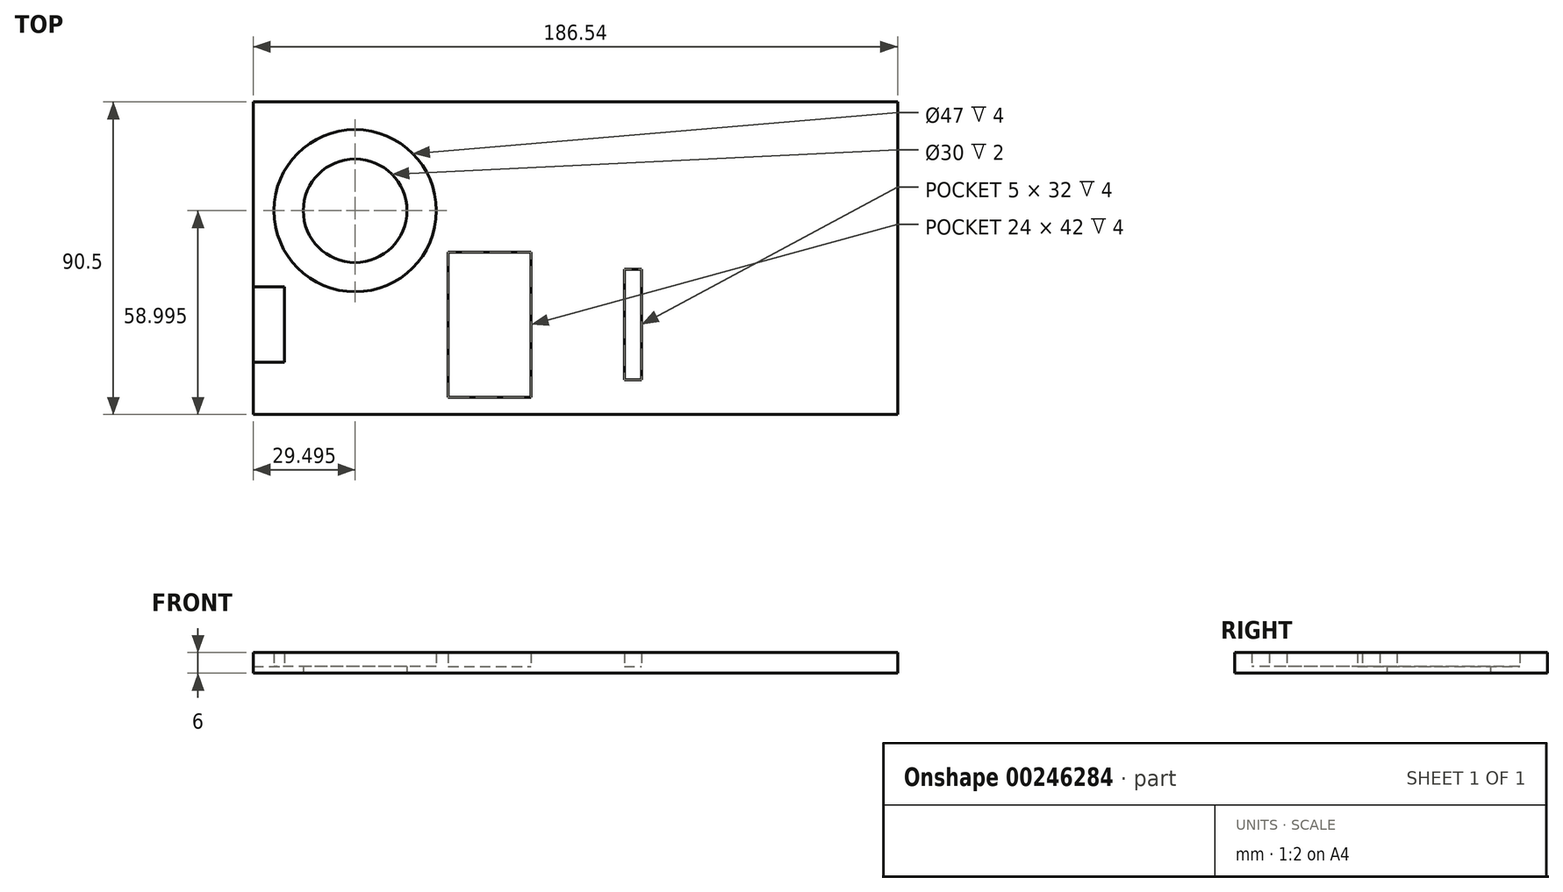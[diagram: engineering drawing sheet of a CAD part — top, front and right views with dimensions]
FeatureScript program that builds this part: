
annotation { "Feature Type Name" : "Feature", "Feature Type Description" : "" }
export const myFeature = defineFeature(function(context is Context, id is Id, definition is map)
    precondition{}
    {
        {
            var Q0;
            Q0=qCreatedBy(makeId("Top.planeOp"),FACE);
            var sketch = newSketch(context, id + "F0", { "sketchPlane" : qUnion([Q0])});
            skLineSegment(sketch, "E0.bottom", {"start": v(-93.27, 69.1) * mm, "end": v(93.27, 69.1) * mm});
            skLineSegment(sketch, "E0.top", {"start": v(-93.27, -21.4) * mm, "end": v(93.27, -21.4) * mm});
            skLineSegment(sketch, "E0.left", {"start": v(-93.27, 69.1) * mm, "end": v(-93.27, -21.4) * mm});
            skLineSegment(sketch, "E0.right", {"start": v(93.27, 69.1) * mm, "end": v(93.27, -21.4) * mm});
            skPoint(sketch, "E1", {"position": v(0, 69.1) * mm});
            skCircle(sketch, "E2", {"center": v(-63.77, 37.6) * mm, "radius": 26.5 * mm, "construction": true});
            skLineSegment(sketch, "E3", {"start": v(-52.33, 4.6) * mm, "end": v(-1.02, 4.6) * mm, "construction": true});
            skLineSegment(sketch, "E4.bottom", {"start": v(-79.77, 13.6) * mm, "end": v(-47.77, 13.6) * mm, "construction": true});
            skLineSegment(sketch, "E4.top", {"start": v(-79.77, -4.4) * mm, "end": v(-47.77, -4.4) * mm, "construction": true});
            skLineSegment(sketch, "E4.left", {"start": v(-79.77, 13.6) * mm, "end": v(-79.77, -4.4) * mm, "construction": true});
            skLineSegment(sketch, "E4.right", {"start": v(-47.77, 13.6) * mm, "end": v(-47.77, -4.4) * mm, "construction": true});
            skPoint(sketch, "E5", {"position": v(-47.77, 4.6) * mm});
            skPoint(sketch, "E6", {"position": v(-63.77, -4.4) * mm});
            skLineSegment(sketch, "E7.bottom", {"start": v(14.17, 20.6) * mm, "end": v(19.17, 20.6) * mm});
            skLineSegment(sketch, "E7.top", {"start": v(14.17, -11.4) * mm, "end": v(19.17, -11.4) * mm});
            skLineSegment(sketch, "E7.left", {"start": v(14.17, 20.6) * mm, "end": v(14.17, -11.4) * mm});
            skLineSegment(sketch, "E7.right", {"start": v(93.27, 20.6) * mm, "end": v(93.27, -11.4) * mm});
            skLineSegment(sketch, "E8.bottom", {"start": v(-93.27, 15.5) * mm, "end": v(-84.27, 15.5) * mm});
            skLineSegment(sketch, "E8.top", {"start": v(-93.27, -6.29) * mm, "end": v(-84.27, -6.29) * mm});
            skLineSegment(sketch, "E8.left", {"start": v(-93.27, 15.5) * mm, "end": v(-93.27, -6.29) * mm});
            skLineSegment(sketch, "E8.right", {"start": v(-84.27, 15.5) * mm, "end": v(-84.27, -6.29) * mm});
            skPoint(sketch, "E9", {"position": v(-84.27, 4.6) * mm});
            skPoint(sketch, "E10.firstSnap0", {"position": v(-88.77, 15.5) * mm});
            skLineSegment(sketch, "E11.bottom", {"start": v(-15.83, 13.6) * mm, "end": v(14.17, 13.6) * mm, "construction": true});
            skLineSegment(sketch, "E11.top", {"start": v(-15.83, -4.4) * mm, "end": v(14.17, -4.4) * mm, "construction": true});
            skLineSegment(sketch, "E11.left", {"start": v(-15.83, 13.6) * mm, "end": v(-15.83, -4.4) * mm});
            skLineSegment(sketch, "E11.right", {"start": v(14.17, 13.6) * mm, "end": v(14.17, -4.4) * mm});
            skPoint(sketch, "E12", {"position": v(14.17, 4.6) * mm});
            skPoint(sketch, "E13", {"position": v(93.27, 4.6) * mm});
            skLineSegment(sketch, "E14.bottom", {"start": v(-33.83, 25.6) * mm, "end": v(-15.83, 25.6) * mm});
            skLineSegment(sketch, "E14.top", {"start": v(-33.83, -16.4) * mm, "end": v(-15.83, -16.4) * mm});
            skLineSegment(sketch, "E14.left", {"start": v(-33.83, 25.6) * mm, "end": v(-33.83, -16.4) * mm, "construction": true});
            skLineSegment(sketch, "E14.right", {"start": v(-15.83, 25.6) * mm, "end": v(-15.83, -16.4) * mm, "construction": true});
            skPoint(sketch, "E15", {"position": v(-33.83, 4.6) * mm});
            skLineSegment(sketch, "E16.left", {"start": v(-47.77, 9.6) * mm, "end": v(-47.77, -0.4) * mm});
            skLineSegment(sketch, "E16.right", {"start": v(-33.83, 9.6) * mm, "end": v(-33.83, -0.4) * mm});
            skLineSegment(sketch, "E17", {"start": v(-15.83, 25.6) * mm, "end": v(-12.83, 25.6) * mm});
            skLineSegment(sketch, "E18", {"start": v(-12.83, 25.6) * mm, "end": v(-12.83, -16.4) * mm});
            skLineSegment(sketch, "E19", {"start": v(-12.83, -16.4) * mm, "end": v(-15.83, -16.4) * mm});
            skLineSegment(sketch, "E20", {"start": v(-33.83, 25.6) * mm, "end": v(-36.83, 25.6) * mm});
            skLineSegment(sketch, "E21", {"start": v(-36.83, 25.6) * mm, "end": v(-36.83, -16.4) * mm});
            skLineSegment(sketch, "E22", {"start": v(-36.83, -16.4) * mm, "end": v(-33.83, -16.4) * mm});
            skLineSegment(sketch, "E23", {"start": v(-36.83, 25.6) * mm, "end": v(-39.57, 26.83) * mm, "construction": true});
            skLineSegment(sketch, "E24.bottom", {"start": v(-41.83, 9.6) * mm, "end": v(-33.83, 9.6) * mm, "construction": true});
            skLineSegment(sketch, "E24.top", {"start": v(-41.83, -0.4) * mm, "end": v(-33.83, -0.4) * mm, "construction": true});
            skLineSegment(sketch, "E24.left", {"start": v(-41.83, 9.6) * mm, "end": v(-41.83, -0.4) * mm, "construction": true});
            skCircle(sketch, "E25", {"center": v(-63.77, 37.6) * mm, "radius": 15 * mm});
            skLineSegment(sketch, "E26", {"start": v(19.17, 20.6) * mm, "end": v(19.17, -11.4) * mm});
            skCircle(sketch, "E27", {"center": v(-63.77, 37.6) * mm, "radius": 23.5 * mm});
            skSolve(sketch);
        }
        {
            var Q0;
            {var subQ15=sQuery(id+"F0.wireOp",EDGE,"E0.bottom");Q0=makeQuery(id+"F0.imprint","IMPRINT",FACE,{"disambiguationData":[TD([[makeQuery(id+"F0.imprint","IMPRINT",EDGE,{"derivedFrom":subQ15}),-1.0]])]});}
            extrude(context, id + "F1", {"entities" : qUnion([Q0]), "depth" : 6 * mm});
        }
        {
            var Q0;
            Q0=makeQuery(id+"F0.imprint","IMPRINT",FACE,{"disambiguationData":[TD([[makeQuery(id+"F0.imprint","IMPRINT",EDGE,{"derivedFrom":sQuery(id+"F0.wireOp",EDGE,"E25")}),-1.0]])]});
            var Q1;
            Q1=makeQuery(id+"F0.imprint","IMPRINT",FACE,{"disambiguationData":[TD([[makeQuery(id+"F0.imprint","IMPRINT",EDGE,{"derivedFrom":sQuery(id+"F0.wireOp",EDGE,"E8.bottom")}),-1.0]])]});
            var Q2;
            {var subQ3=sQuery(id+"F0.wireOp",EDGE,"E14.bottom");Q2=makeQuery(id+"F0.imprint","IMPRINT",FACE,{"disambiguationData":[TD([[makeQuery(id+"F0.imprint","IMPRINT",EDGE,{"derivedFrom":subQ3}),-1.0]])]});}
            var Q3;
            {var subQ3=sQuery(id+"F0.wireOp",EDGE,"E7.bottom");Q3=makeQuery(id+"F0.imprint","IMPRINT",FACE,{"disambiguationData":[TD([[makeQuery(id+"F0.imprint","IMPRINT",EDGE,{"derivedFrom":subQ3}),-1.0]])]});}
            extrude(context, id + "F2", {"entities" : qUnion([Q0, Q1, Q2, Q3]), "operationType" : NewBodyOperationType.ADD, "depth" : 2 * mm});
        }
    });
